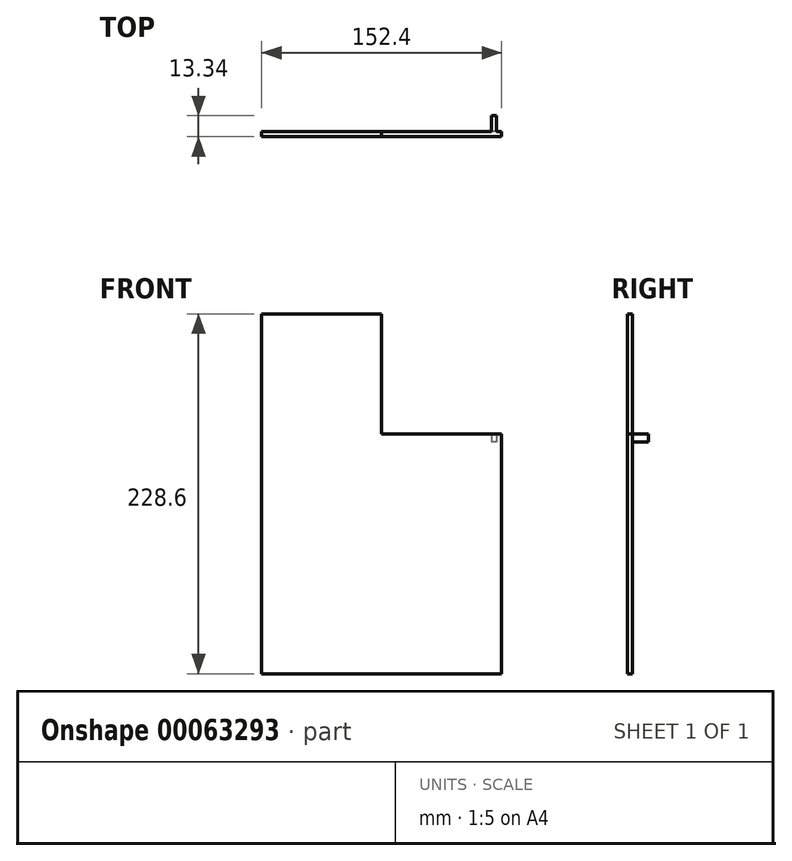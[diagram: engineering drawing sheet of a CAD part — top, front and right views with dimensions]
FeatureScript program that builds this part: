
annotation { "Feature Type Name" : "Feature", "Feature Type Description" : "" }
export const myFeature = defineFeature(function(context is Context, id is Id, definition is map)
    precondition{}
    {
        {
            var Q0;
            Q0=qCreatedBy(makeId("Front.planeOp"),FACE);
            var sketch = newSketch(context, id + "F0", { "sketchPlane" : qUnion([Q0])});
            skLineSegment(sketch, "E0.rect.bottom", {"start": v(76.2, 114.3) * mm, "end": v(-76.2, 114.3) * mm});
            skLineSegment(sketch, "E0.rect.top", {"start": v(76.2, -114.3) * mm, "end": v(-76.2, -114.3) * mm});
            skLineSegment(sketch, "E0.rect.left", {"start": v(76.2, 114.3) * mm, "end": v(76.2, -114.3) * mm});
            skLineSegment(sketch, "E0.rect.right", {"start": v(-76.2, 114.3) * mm, "end": v(-76.2, -114.3) * mm});
            skPoint(sketch, "E0.rect.middle", {"position": v(0, 0) * mm});
            skSolve(sketch);
        }
        {
            var Q0;
            Q0=makeQuery(id+"F0.imprint","IMPRINT",FACE,{"disambiguationData":[TD([[makeQuery(id+"F0.imprint","IMPRINT",EDGE,{"derivedFrom":sQuery(id+"F0.wireOp",EDGE,"E0.rect.bottom")}),1.0]])]});
            extrude(context, id + "F1", {"entities" : qUnion([Q0]), "depth" : 3.17 * mm, "symmetric" : true});
        }
        {
            var Q0;
            Q0=makeQuery(id+"F1.opExtrude","CAP_FACE",FACE,{"disambiguationData":[OSD([sQuery(id+"F0.wireOp",EDGE,"E0.rect.bottom"),sQuery(id+"F0.wireOp",EDGE,"E0.rect.top"),sQuery(id+"F0.wireOp",EDGE,"E0.rect.left"),sQuery(id+"F0.wireOp",EDGE,"E0.rect.right")])],"isStart":false});
            var sketch = newSketch(context, id + "F2", { "sketchPlane" : qUnion([Q0])});
            skLineSegment(sketch, "E1.bottom", {"start": v(76.2, 114.3) * mm, "end": v(0, 114.3) * mm});
            skLineSegment(sketch, "E1.top", {"start": v(76.2, 38.1) * mm, "end": v(0, 38.1) * mm});
            skLineSegment(sketch, "E1.left", {"start": v(76.2, 114.3) * mm, "end": v(76.2, 38.1) * mm});
            skLineSegment(sketch, "E1.right", {"start": v(0, 114.3) * mm, "end": v(0, 38.1) * mm});
            skSolve(sketch);
        }
        {
            var Q0;
            Q0 = qSketchRegion(id + "F2", true);
            extrude(context, id + "F3", {"entities" : qUnion([Q0]), "operationType" : NewBodyOperationType.REMOVE, "endBound" : BoundingType.THROUGH_ALL, "oppositeDirection" : true, "depth" : 25.4 * mm});
        }
        {
            var Q0;
            Q0=makeQuery(id+"F1.opExtrude","CAP_FACE",FACE,{"disambiguationData":[OSD([sQuery(id+"F0.wireOp",EDGE,"E0.rect.bottom"),sQuery(id+"F0.wireOp",EDGE,"E0.rect.top"),sQuery(id+"F0.wireOp",EDGE,"E0.rect.left"),sQuery(id+"F0.wireOp",EDGE,"E0.rect.right")])],"isStart":true});
            var sketch = newSketch(context, id + "F4", { "sketchPlane" : qUnion([Q0])});
            skLineSegment(sketch, "E2.bottom", {"start": v(-73.03, 38.1) * mm, "end": v(-69.85, 38.1) * mm});
            skLineSegment(sketch, "E2.top", {"start": v(-73.03, 32.95) * mm, "end": v(-69.85, 32.95) * mm});
            skLineSegment(sketch, "E2.left", {"start": v(-73.03, 38.1) * mm, "end": v(-73.03, 32.95) * mm});
            skLineSegment(sketch, "E2.right", {"start": v(-69.85, 38.1) * mm, "end": v(-69.85, 32.95) * mm});
            skSolve(sketch);
        }
        {
            var Q0;
            Q0=makeQuery(id+"F4.imprint","IMPRINT",FACE,{"disambiguationData":[TD([[makeQuery(id+"F4.imprint","IMPRINT",EDGE,{"derivedFrom":sQuery(id+"F4.wireOp",EDGE,"E2.bottom")}),-1.0]])]});
            extrude(context, id + "F5", {"entities" : qUnion([Q0]), "operationType" : NewBodyOperationType.ADD, "depth" : 10.16 * mm});
        }
    });
